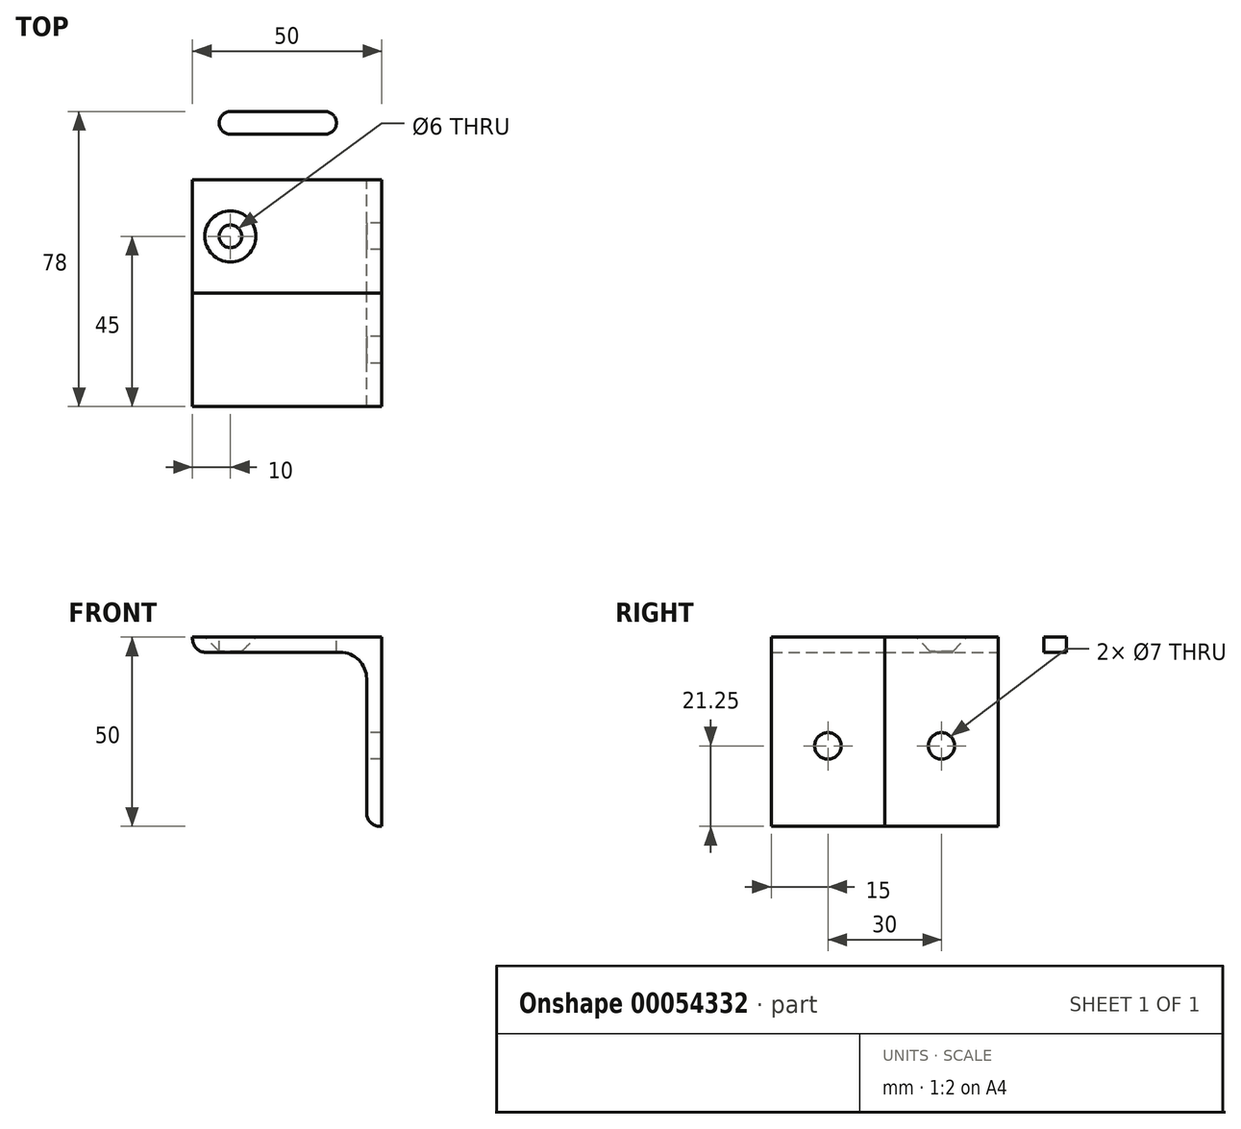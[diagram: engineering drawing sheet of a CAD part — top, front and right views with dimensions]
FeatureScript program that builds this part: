
annotation { "Feature Type Name" : "Feature", "Feature Type Description" : "" }
export const myFeature = defineFeature(function(context is Context, id is Id, definition is map)
    precondition{}
    {
        {
            var Q0;
            Q0=qCreatedBy(makeId("Front.planeOp"),FACE);
            var sketch = newSketch(context, id + "F0", { "sketchPlane" : qUnion([Q0])});
            skLineSegment(sketch, "E0", {"start": v(0, 0) * mm, "end": v(-50, 0) * mm});
            skLineSegment(sketch, "E1", {"start": v(-50, 0) * mm, "end": v(-50, -0.5) * mm});
            skLineSegment(sketch, "E2", {"start": v(-0.5, -50) * mm, "end": v(0, -50) * mm});
            skLineSegment(sketch, "E3", {"start": v(0, -50) * mm, "end": v(0, 0) * mm});
            skLineSegment(sketch, "E4.0", {"start": v(-11, -4) * mm, "end": v(-46.5, -4) * mm});
            skLineSegment(sketch, "E4.1", {"start": v(-4, -46.5) * mm, "end": v(-4, -11) * mm});
            skArc(sketch, "E5", {"start": v(-4, -11) * mm, "mid": v(-6.05, -6.05) * mm, "end": v(-11, -4) * mm});
            skArc(sketch, "E6", {"start": v(-50, -0.5) * mm, "mid": v(-48.97, -2.97) * mm, "end": v(-46.5, -4) * mm});
            skArc(sketch, "E7", {"start": v(-4, -46.5) * mm, "mid": v(-2.97, -48.97) * mm, "end": v(-0.5, -50) * mm});
            skSolve(sketch);
        }
        {
            var Q0;
            Q0=makeQuery(id+"F0.imprint","IMPRINT",FACE,{"disambiguationData":[TD([[makeQuery(id+"F0.imprint","IMPRINT",EDGE,{"derivedFrom":sQuery(id+"F0.wireOp",EDGE,"E0")}),1.0]])]});
            extrude(context, id + "F1", {"entities" : qUnion([Q0]), "depth" : 30 * mm});
        }
        {
            var Q0;
            Q0=makeQuery(id+"F1.opExtrude","SWEPT_FACE",FACE,{"disambiguationData":[OSD([sQuery(id+"F0.wireOp",EDGE,"E4.1")])]});
            var sketch = newSketch(context, id + "F2", { "sketchPlane" : qUnion([Q0])});
            skLineSegment(sketch, "E8", {"start": v(0, -46.5) * mm, "end": v(30, -11) * mm, "construction": true});
            skPoint(sketch, "E9", {"position": v(15, -28.75) * mm});
            skSolve(sketch);
        }
        {
            var Q0;
            Q0=sQuery(id+"F2.wireOp",VERTEX,"E9");
            var Q1;
            Q1=makeQuery(id+"F1.opExtrude","SWEPT_BODY",BODY,{"disambiguationData":[OSD([sQuery(id+"F0.wireOp",EDGE,"E0"),sQuery(id+"F0.wireOp",EDGE,"E1"),sQuery(id+"F0.wireOp",EDGE,"E2"),sQuery(id+"F0.wireOp",EDGE,"E3"),sQuery(id+"F0.wireOp",EDGE,"E4.0"),sQuery(id+"F0.wireOp",EDGE,"E4.1"),sQuery(id+"F0.wireOp",EDGE,"E5"),sQuery(id+"F0.wireOp",EDGE,"E6"),sQuery(id+"F0.wireOp",EDGE,"E7")])]});
            hole(context, id + "F3", {"style" : HoleStyle.SIMPLE, "holeDiameter" : 7 * mm, "endStyle" : HoleEndStyle.THROUGH, "locations" : qUnion([Q0]), "scope" : qUnion([Q1])});
        }
        {
            var Q0;
            Q0=makeQuery(id+"F1.opExtrude","SWEPT_FACE",FACE,{"disambiguationData":[OSD([sQuery(id+"F0.wireOp",EDGE,"E0")])]});
            var sketch = newSketch(context, id + "F4", { "sketchPlane" : qUnion([Q0])});
            skPoint(sketch, "E10", {"position": v(-40, -15) * mm});
            skSolve(sketch);
        }
        {
            var Q0;
            Q0=sQuery(id+"F4.wireOp",VERTEX,"E10");
            var Q1;
            Q1=makeQuery(id+"F1.opExtrude","SWEPT_BODY",BODY,{"disambiguationData":[OSD([sQuery(id+"F0.wireOp",EDGE,"E0"),sQuery(id+"F0.wireOp",EDGE,"E1"),sQuery(id+"F0.wireOp",EDGE,"E2"),sQuery(id+"F0.wireOp",EDGE,"E3"),sQuery(id+"F0.wireOp",EDGE,"E4.0"),sQuery(id+"F0.wireOp",EDGE,"E4.1"),sQuery(id+"F0.wireOp",EDGE,"E5"),sQuery(id+"F0.wireOp",EDGE,"E6"),sQuery(id+"F0.wireOp",EDGE,"E7")])]});
            hole(context, id + "F5", {"style" : HoleStyle.C_SINK, "holeDiameter" : 6 * mm, "cSinkDiameter" : 13.5 * mm, "endStyle" : HoleEndStyle.THROUGH, "locations" : qUnion([Q0]), "scope" : qUnion([Q1]), "cSinkAngle" : 90 * degree});
        }
        {
            var Q0;
            Q0 = qSketchRegion(id + "F0", true);
            extrude(context, id + "F6", {"entities" : qUnion([Q0]), "oppositeDirection" : true, "depth" : 30 * mm});
        }
        {
            var Q0;
            Q0=makeQuery(id+"F6.opExtrude","SWEPT_FACE",FACE,{"disambiguationData":[OSD([sQuery(id+"F0.wireOp",EDGE,"E0")])]});
            var sketch = newSketch(context, id + "F7", { "sketchPlane" : qUnion([Q0])});
            skLineSegment(sketch, "E11", {"start": v(-40, 15) * mm, "end": v(-15, 15) * mm, "construction": true});
            skPoint(sketch, "E11.startSnap0", {"position": v(-50, 15) * mm});
            skArc(sketch, "E12.0.startCap", {"start": v(-40, 12) * mm, "mid": v(-43, 15) * mm, "end": v(-40, 18) * mm});
            skArc(sketch, "E12.0.endCap", {"start": v(-15, 18) * mm, "mid": v(-12, 15) * mm, "end": v(-15, 12) * mm});
            skLineSegment(sketch, "E12.0.left", {"start": v(-40, 18) * mm, "end": v(-15, 18) * mm});
            skLineSegment(sketch, "E12.0.right", {"start": v(-40, 12) * mm, "end": v(-15, 12) * mm});
            skSolve(sketch);
        }
        {
            var Q0;
            Q0=makeQuery(id+"F7.imprint","IMPRINT",FACE,{"disambiguationData":[TD([[makeQuery(id+"F7.imprint","IMPRINT",EDGE,{"derivedFrom":sQuery(id+"F7.wireOp",EDGE,"E12.0.startCap")}),-1.0]])]});
            extrude(context, id + "F8", {"entities" : qUnion([Q0]), "operationType" : NewBodyOperationType.REMOVE, "endBound" : BoundingType.THROUGH_ALL, "oppositeDirection" : true, "depth" : 25 * mm});
        }
        {
            var Q0;
            Q0=makeQuery(id+"F1.opExtrude","CAP_FACE",FACE,{"disambiguationData":[OSD([sQuery(id+"F0.wireOp",EDGE,"E0"),sQuery(id+"F0.wireOp",EDGE,"E1"),sQuery(id+"F0.wireOp",EDGE,"E2"),sQuery(id+"F0.wireOp",EDGE,"E3"),sQuery(id+"F0.wireOp",EDGE,"E4.0"),sQuery(id+"F0.wireOp",EDGE,"E4.1"),sQuery(id+"F0.wireOp",EDGE,"E5"),sQuery(id+"F0.wireOp",EDGE,"E6"),sQuery(id+"F0.wireOp",EDGE,"E7")])],"isStart":false});
            extrude(context, id + "F9", {"entities" : qUnion([Q0]), "depth" : 30 * mm});
        }
        {
            var Q0;
            Q0=makeQuery(id+"F9.opExtrude","SWEPT_FACE",FACE,{"disambiguationData":[OSD([sQuery(id+"F0.wireOp",EDGE,"E4.1")])]});
            var sketch = newSketch(context, id + "F10", { "sketchPlane" : qUnion([Q0])});
            skLineSegment(sketch, "E13", {"start": v(60, -11) * mm, "end": v(30, -46.5) * mm, "construction": true});
            skPoint(sketch, "E14", {"position": v(45, -28.75) * mm});
            skSolve(sketch);
        }
        {
            var Q0;
            Q0=sQuery(id+"F10.wireOp",VERTEX,"E14");
            var Q1;
            Q1=makeQuery(id+"F9.opExtrude","SWEPT_BODY",BODY,{"disambiguationData":[OSD([sQuery(id+"F0.wireOp",EDGE,"E0"),sQuery(id+"F0.wireOp",EDGE,"E1"),sQuery(id+"F0.wireOp",EDGE,"E2"),sQuery(id+"F0.wireOp",EDGE,"E3"),sQuery(id+"F0.wireOp",EDGE,"E4.0"),sQuery(id+"F0.wireOp",EDGE,"E4.1"),sQuery(id+"F0.wireOp",EDGE,"E5"),sQuery(id+"F0.wireOp",EDGE,"E6"),sQuery(id+"F0.wireOp",EDGE,"E7")])]});
            hole(context, id + "F11", {"style" : HoleStyle.SIMPLE, "holeDiameter" : 7 * mm, "endStyle" : HoleEndStyle.THROUGH, "locations" : qUnion([Q0]), "scope" : qUnion([Q1])});
        }
    });
